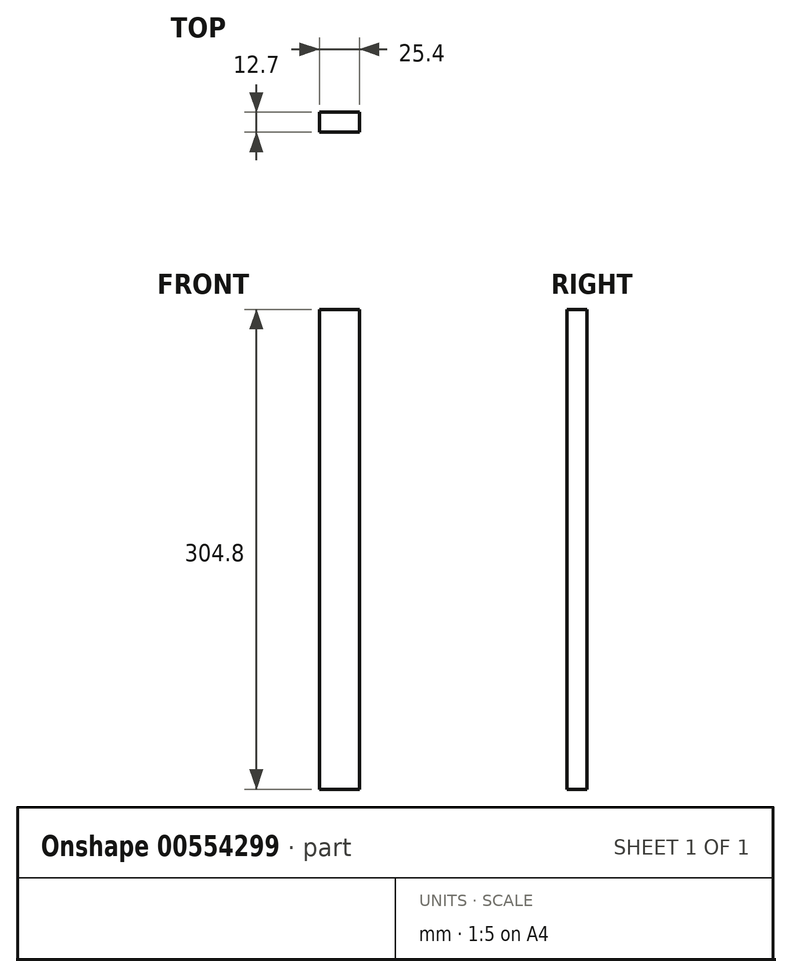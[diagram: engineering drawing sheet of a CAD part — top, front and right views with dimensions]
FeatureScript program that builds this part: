
annotation { "Feature Type Name" : "Feature", "Feature Type Description" : "" }
export const myFeature = defineFeature(function(context is Context, id is Id, definition is map)
    precondition{}
    {
        {
            var Q0;
            Q0=qCreatedBy(makeId("Front.planeOp"),FACE);
            var sketch = newSketch(context, id + "F0", { "sketchPlane" : qUnion([Q0])});
            skLineSegment(sketch, "E0.bottom", {"start": v(-13.28, 170.26) * mm, "end": v(12.12, 170.26) * mm});
            skLineSegment(sketch, "E0.top", {"start": v(-13.28, -134.54) * mm, "end": v(12.12, -134.54) * mm});
            skLineSegment(sketch, "E0.left", {"start": v(-13.28, 170.26) * mm, "end": v(-13.28, -134.54) * mm});
            skLineSegment(sketch, "E0.right", {"start": v(12.12, 170.26) * mm, "end": v(12.12, -134.54) * mm});
            skSolve(sketch);
        }
        {
            var Q0;
            Q0 = qSketchRegion(id + "F0", true);
            extrude(context, id + "F1", {"entities" : qUnion([Q0]), "depth" : 12.7 * mm, "offsetDistance" : 25.4 * mm});
        }
    });
